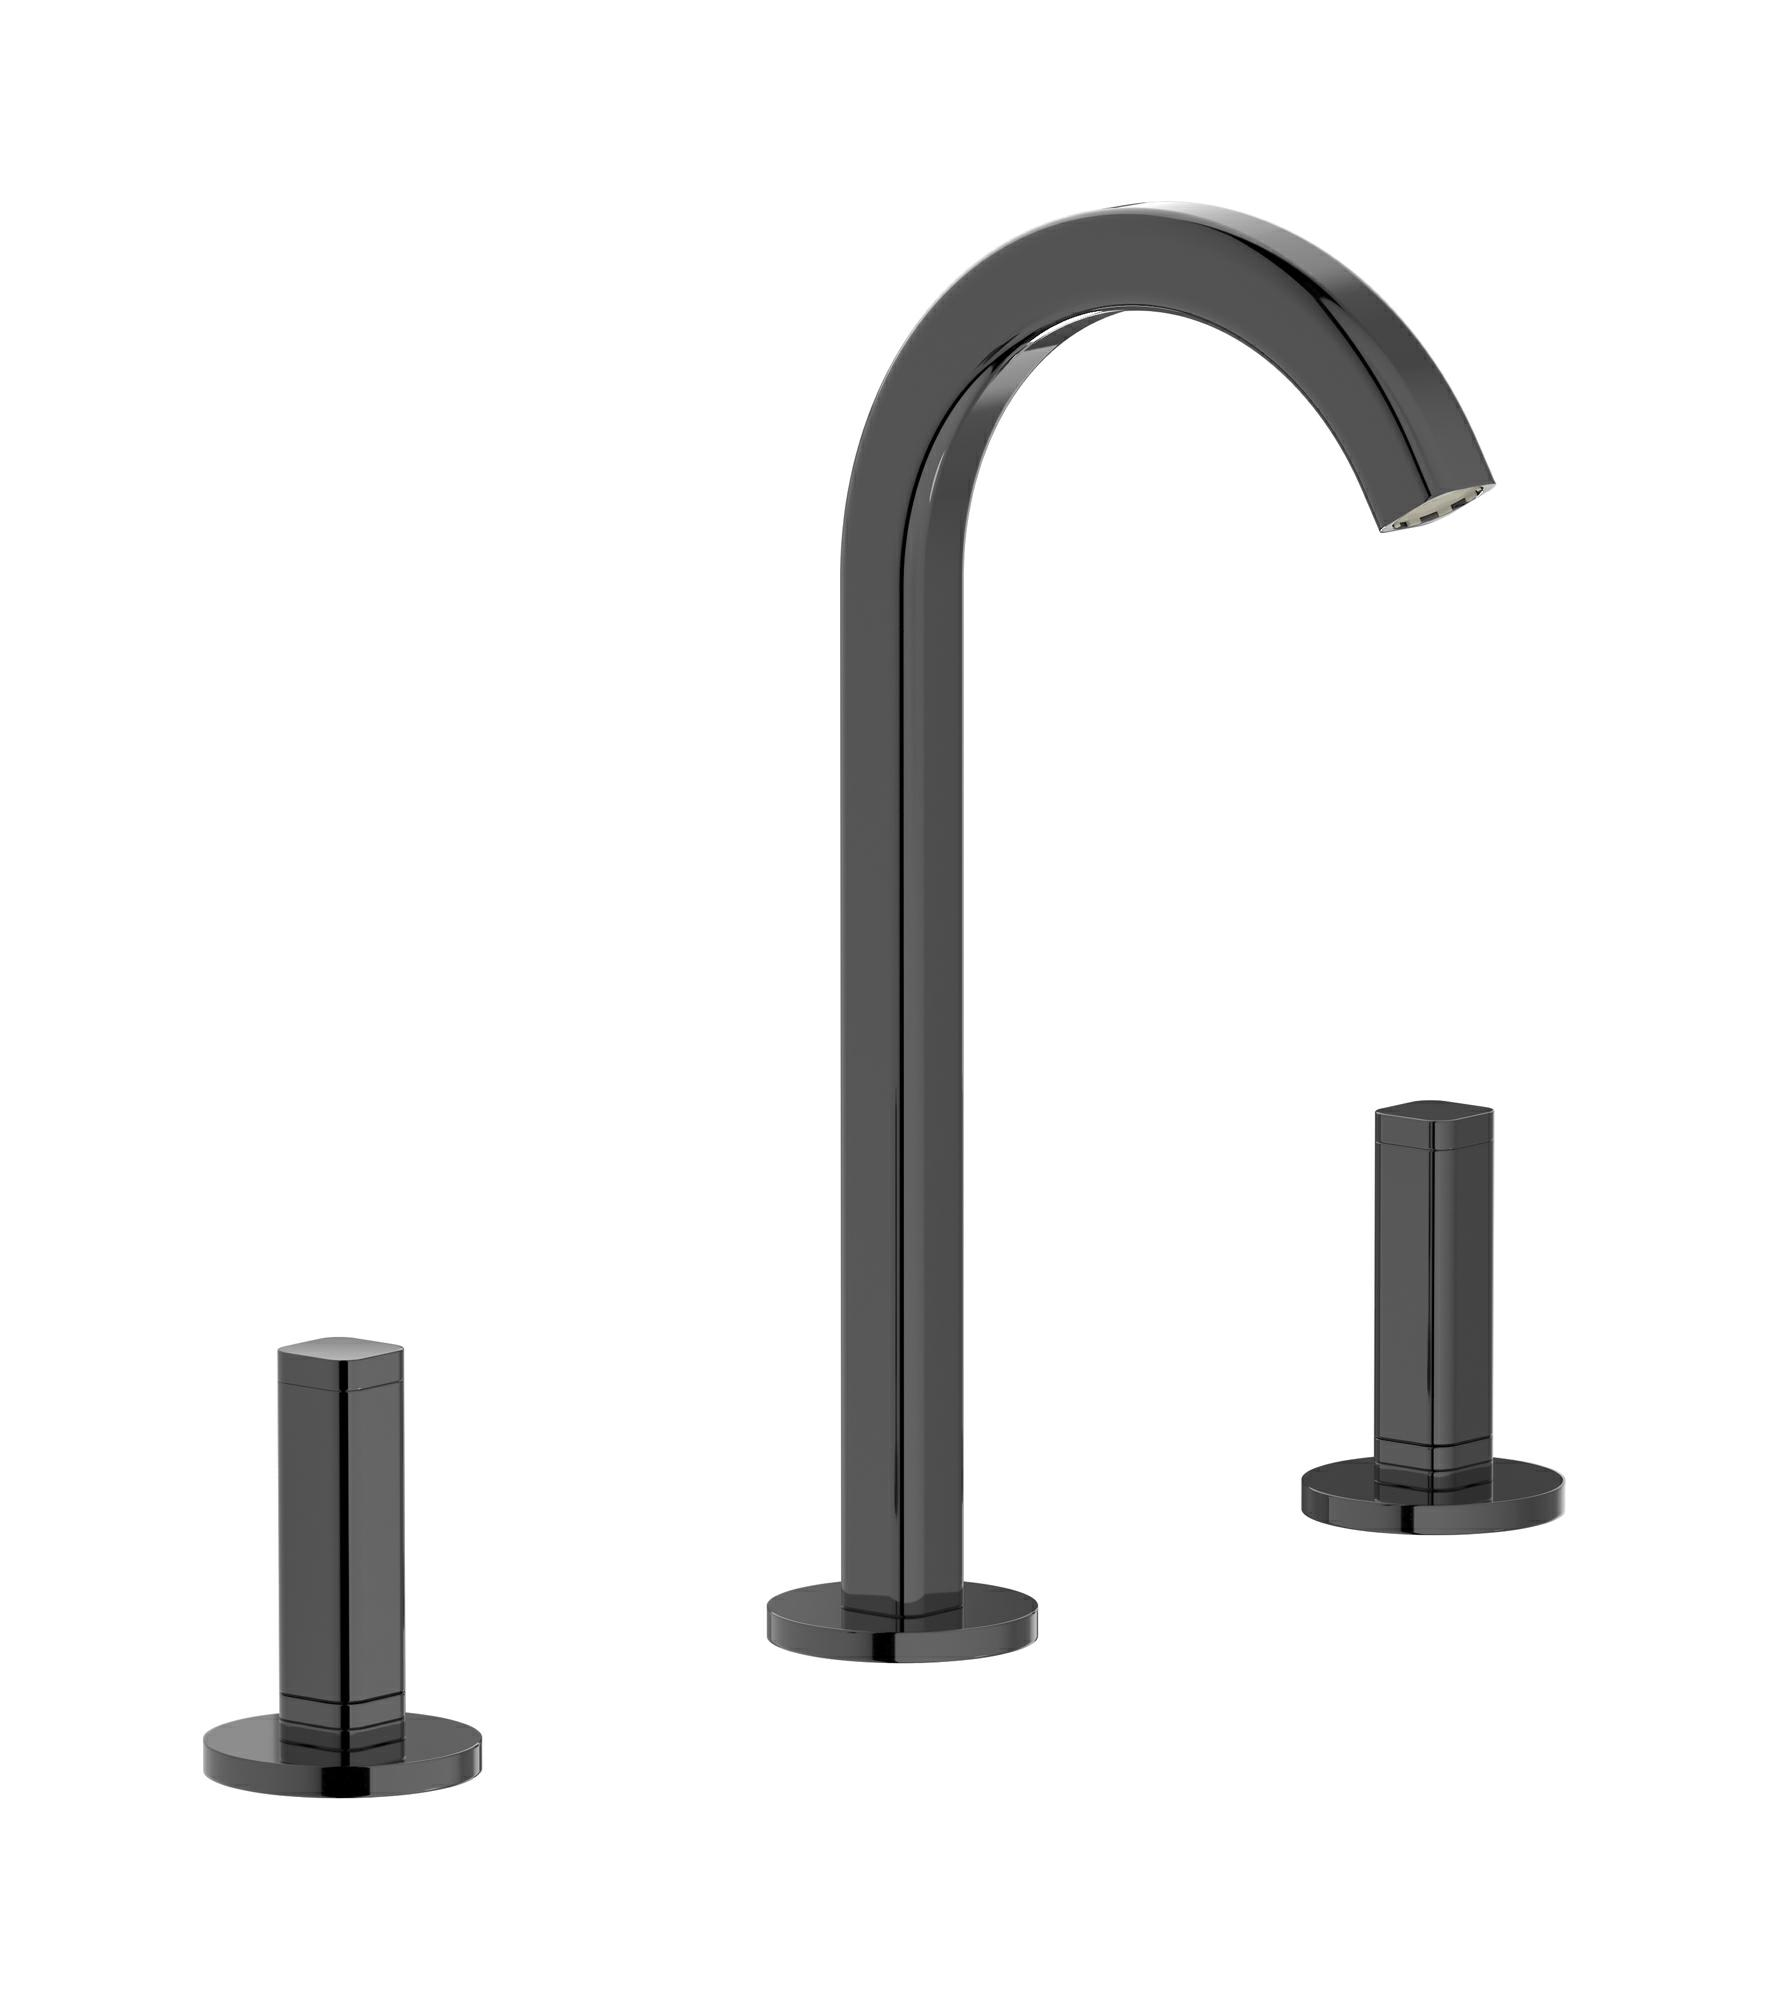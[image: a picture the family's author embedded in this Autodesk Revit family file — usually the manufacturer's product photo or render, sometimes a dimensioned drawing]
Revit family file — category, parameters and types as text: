
# Revit family: EI392_1
name_source: partatom
category: Apparecchi idraulici
units: mm (PartAtom-declared; Revit-internal decimal feet)

## family parameters
Basato su piano di lavoro = No
Condiviso = No
Mantieni orientamento annotazione = No
Numero OmniClass = 23.45.55.17
Punto di calcolo locali = No
Quota connettore circolare = Usa diametro
Sempre verticale = Sì
Taglio con vuoti quando caricato = No
Tipo di parte = Normale
Titolo OmniClass = Mixing Faucets

## types (12) — shared parameters
Cold water inlet = 10 mm  [stored 0.0328084 ft]
Commenti sul tipo = Washbasin
Connessione CW = No
Connessione HW = No
Connessione di scarico = No
Connessione di ventilazione = No
Descrizione = Three hole washbasin set complete
Hot water inlet = 10 mm  [stored 0.0328084 ft]
Produttore = IB Rubinetterie S.p.A.
URL = https://www.weareib.it
zero-valued in all types: Prospetto di default

## per-type parameters (varying)
| type | Finishes surface | Immagine tipo | Modello |
| Chrome | IB_Chrome | EI392CC_1.jpg | EI392CC_1 |
| Brushed nickel | IB_Brushed nickel | EI392SS_1.jpg | EI392SS_1 |
| Natural brass | IB_Brass | EI392ON_1.jpg | EI392ON_1 |
| Matt black | IB_matt black | EI392NP_1.jpg | EI392NP_1 |
| Black chrome | IB_Black chrome | EI392CF_1.jpg | EI392CF_1 |
| Brushed black chrome | IB_Brushed black chrome | EI392CS_1.jpg | EI392CS_1 |
| Pale gold | IB_Pale gold | EI392II_1.jpg | EI392II_1 |
| Brushed pale gold | IB_brushed pale gold | EI392IS_1.jpg | EI392IS_1 |
| Rose gold | IB_Rose gold | EI392RS_1.jpg | EI392RS_1 |
| Brushed rose gold | IB_Brushed rose gold | EI392SR_1.jpg | EI392SR_1 |
| Gold | IB_gold | EI392OO_1.jpg | EI392OO_1 |
| Brushed gold | IB_brushed gold | EI392OS_1.jpg | EI392OS_1 |

note: [stored X ft] marks values corroborated as IEEE doubles in the binary element streams (Revit-internal decimal feet)
